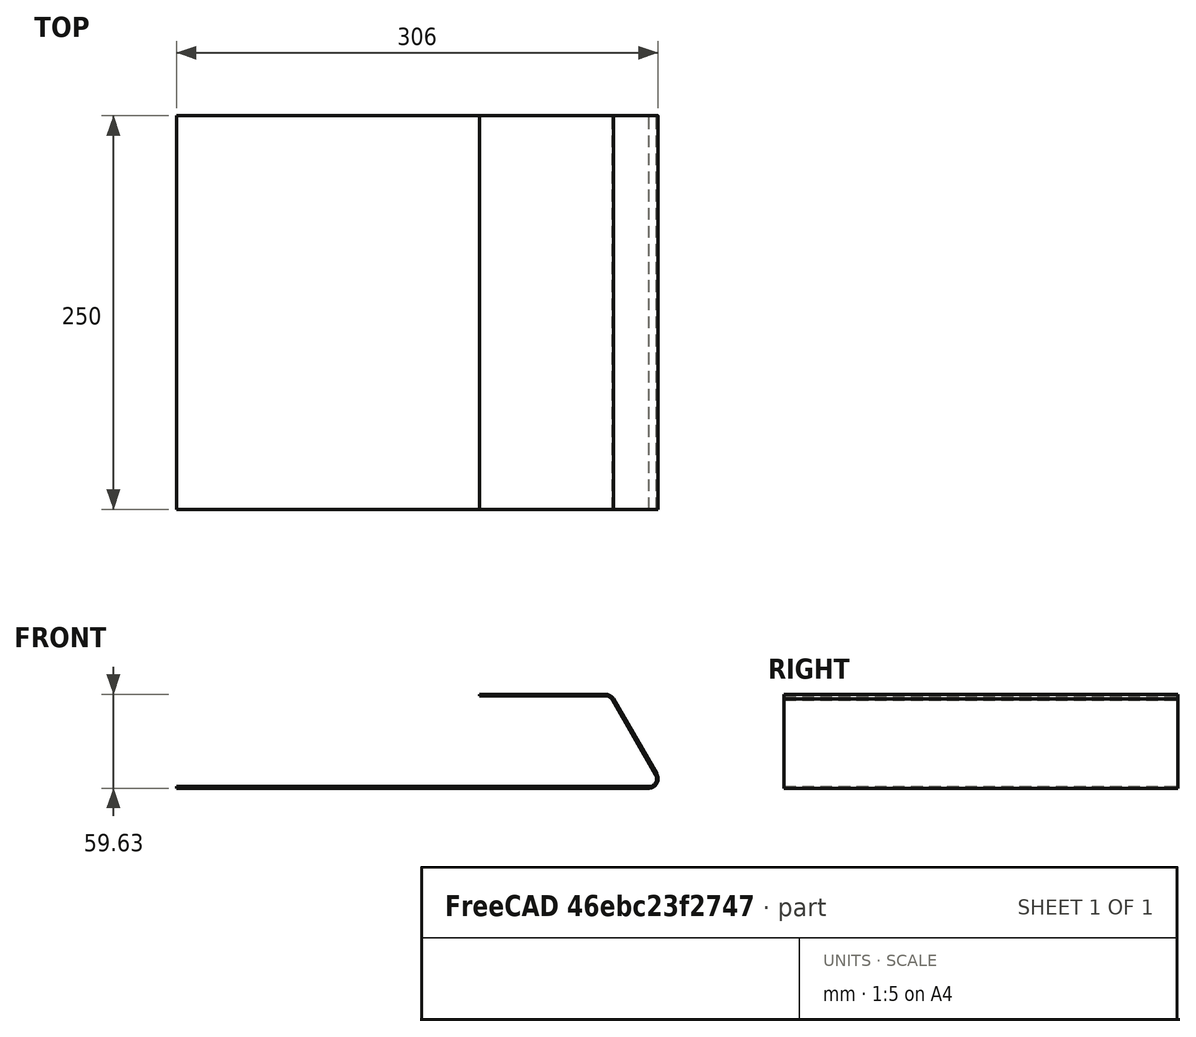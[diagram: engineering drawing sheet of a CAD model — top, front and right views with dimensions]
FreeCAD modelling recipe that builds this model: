
FCSTD DOCUMENT  (FreeCAD 0.20R29177 (Git))
Label: AT_010a_electroDrawer
License: All rights reserved
LicenseURL: http://en.wikipedia.org/wiki/All_rights_reserved
objects: Part::FeaturePython×2, Part::Box×1
note: 3 computed .brp shape members not serialized (recipe doc carries the construction recipe); baked Part::Feature solids carry a one-line shape summary decoded from their .brp

FEATURE [Part::Box] Box  label="Cube"
  AttacherType = Attacher::AttachEngine3D
  Height = 1
  Length = 300
  Width = 250
FEATURE [Part::FeaturePython] Bend  # WARN: FeaturePython — macro-defined, semantics opaque (R4)
  AutoMiter = true
  BendType = 0
  LengthList = [55]
  ReliefFactor = 0.7
  UseReliefFactor = false
  angle = 120
  baseObject = -> Box [Face2]
  bendAList = [120]
  extend1 = 0
  extend2 = 0
  gap1 = 0
  gap2 = 0
  invert = false
  kfactor = 0.5
  length = 55
  maxExtendDist = 5
  minGap = 0.1
  minReliefGap = 1
  miterangle1 = 0
  miterangle2 = 0
  offset = 0
  radius = 5
  reliefType = 0
  reliefd = 1
  reliefw = 0.8
  sketchflip = false
  sketchinvert = false
  unfold = false
FEATURE [Part::FeaturePython] Bend001  # WARN: FeaturePython — macro-defined, semantics opaque (R4)
  AutoMiter = true
  BendType = 0
  LengthList = [80]
  ReliefFactor = 0.7
  UseReliefFactor = false
  angle = 60
  baseObject = -> Bend [Face3]
  bendAList = [60]
  extend1 = 0
  extend2 = 0
  gap1 = 0
  gap2 = 0
  invert = false
  kfactor = 0.5
  length = 80
  maxExtendDist = 5
  minGap = 0.1
  minReliefGap = 1
  miterangle1 = 0
  miterangle2 = 0
  offset = 0
  radius = 5
  reliefType = 0
  reliefd = 1
  reliefw = 0.8
  sketchflip = false
  sketchinvert = false
  unfold = false
